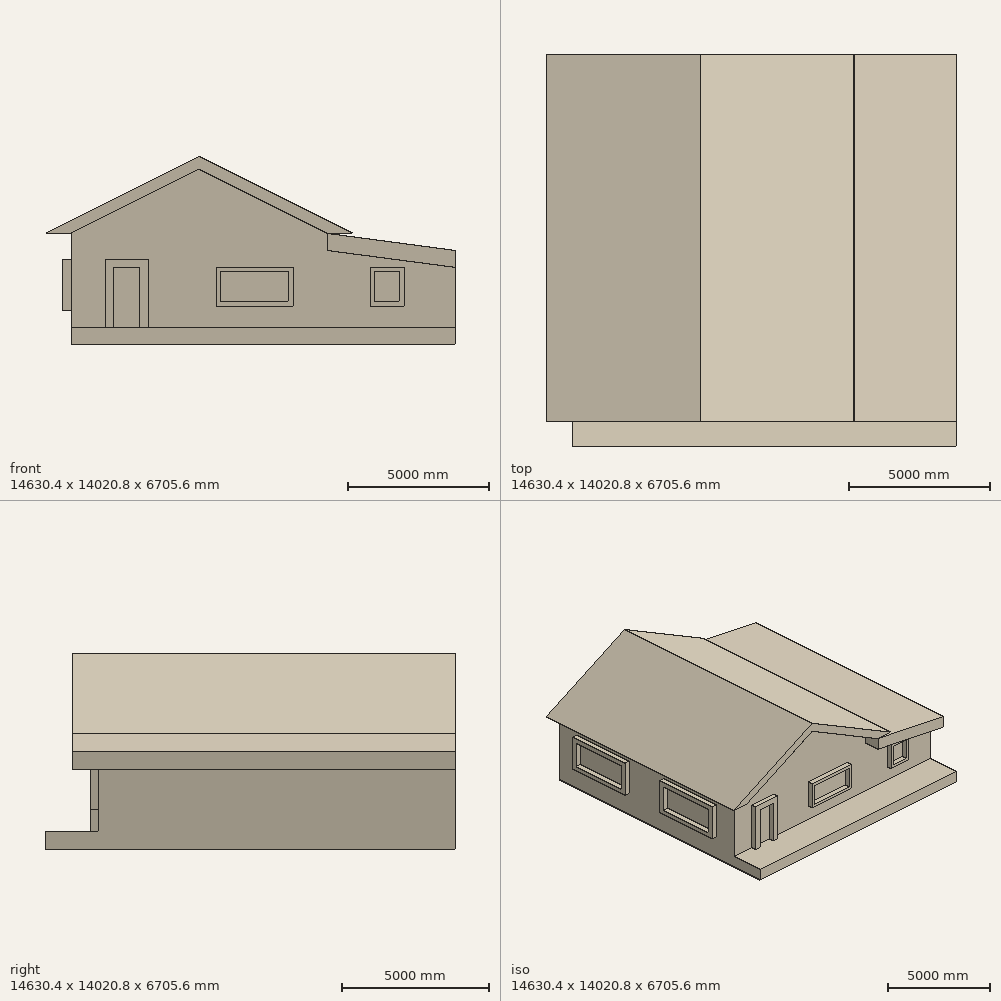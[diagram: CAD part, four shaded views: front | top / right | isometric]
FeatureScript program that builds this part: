
annotation { "Feature Type Name" : "Feature", "Feature Type Description" : "" }
export const myFeature = defineFeature(function(context is Context, id is Id, definition is map)
    precondition{}
    {
        {
            var Q0;
            Q0=qCreatedBy(makeId("Front.planeOp"),FACE);
            var sketch = newSketch(context, id + "F0", { "sketchPlane" : qUnion([Q0])});
            skLineSegment(sketch, "E0", {"start": v(0, 0) * mm, "end": v(-4572, 0) * mm});
            skLineSegment(sketch, "E1", {"start": v(0, 0) * mm, "end": v(4572, 0) * mm});
            skLineSegment(sketch, "E2", {"start": v(0, 0) * mm, "end": v(0, 2286) * mm});
            skLineSegment(sketch, "E3", {"start": v(0, 2286) * mm, "end": v(4572, 0) * mm});
            skLineSegment(sketch, "E4", {"start": v(0, 2286) * mm, "end": v(-4572, 0) * mm});
            skLineSegment(sketch, "E5", {"start": v(4572, 0) * mm, "end": v(5486.4, 0) * mm});
            skLineSegment(sketch, "E6", {"start": v(-4572, 0) * mm, "end": v(-5486.4, 0) * mm});
            skLineSegment(sketch, "E7", {"start": v(0, 2286) * mm, "end": v(0, 2743.2) * mm});
            skLineSegment(sketch, "E8", {"start": v(0, 2743.2) * mm, "end": v(5486.4, 0) * mm});
            skLineSegment(sketch, "E9", {"start": v(0, 2743.2) * mm, "end": v(-5486.4, 0) * mm});
            skLineSegment(sketch, "E10", {"start": v(4572, 0) * mm, "end": v(4572, -3352.8) * mm});
            skLineSegment(sketch, "E11", {"start": v(-4572, 0) * mm, "end": v(-4572, -3352.8) * mm});
            skLineSegment(sketch, "E12", {"start": v(-4572, -3352.8) * mm, "end": v(4572, -3352.8) * mm});
            skLineSegment(sketch, "E13", {"start": v(4572, -3352.8) * mm, "end": v(4572, -3962.4) * mm});
            skLineSegment(sketch, "E14", {"start": v(-4572, -3352.8) * mm, "end": v(-4572, -3962.4) * mm});
            skLineSegment(sketch, "E15", {"start": v(-4572, -3962.4) * mm, "end": v(4572, -3962.4) * mm});
            skLineSegment(sketch, "E16", {"start": v(4572, -3962.4) * mm, "end": v(9144, -3962.4) * mm});
            skLineSegment(sketch, "E17", {"start": v(4572, -3352.8) * mm, "end": v(9144, -3352.8) * mm});
            skLineSegment(sketch, "E18", {"start": v(9144, -3352.8) * mm, "end": v(9144, -3962.4) * mm});
            skLineSegment(sketch, "E19", {"start": v(9144, -3352.8) * mm, "end": v(9144, -609.6) * mm});
            skLineSegment(sketch, "E20", {"start": v(9144, -609.6) * mm, "end": v(4572, 0) * mm});
            skLineSegment(sketch, "E21", {"start": v(4572, -609.6) * mm, "end": v(9144, -1212.83) * mm});
            skLineSegment(sketch, "E22", {"start": v(-3048, -3352.8) * mm, "end": v(-3048, -1219.2) * mm});
            skLineSegment(sketch, "E23", {"start": v(-3048, -1219.2) * mm, "end": v(-2133.6, -1219.2) * mm});
            skLineSegment(sketch, "E24", {"start": v(-2133.6, -1219.2) * mm, "end": v(-2133.6, -3352.8) * mm});
            skLineSegment(sketch, "E25.0", {"start": v(-1828.8, -914.4) * mm, "end": v(-1828.8, -3352.8) * mm});
            skLineSegment(sketch, "E25.1", {"start": v(-3352.8, -914.4) * mm, "end": v(-1828.8, -914.4) * mm});
            skLineSegment(sketch, "E25.2", {"start": v(-3352.8, -3352.8) * mm, "end": v(-3352.8, -914.4) * mm});
            skLineSegment(sketch, "E26", {"start": v(609.6, -1219.2) * mm, "end": v(609.6, -2590.8) * mm});
            skLineSegment(sketch, "E27", {"start": v(609.6, -2590.8) * mm, "end": v(3352.8, -2590.8) * mm});
            skLineSegment(sketch, "E28", {"start": v(3352.8, -2590.8) * mm, "end": v(3352.8, -1219.2) * mm});
            skLineSegment(sketch, "E29", {"start": v(609.6, -1219.2) * mm, "end": v(3352.8, -1219.2) * mm});
            skLineSegment(sketch, "E30.0", {"start": v(3200.4, -2438.4) * mm, "end": v(3200.4, -1371.6) * mm});
            skLineSegment(sketch, "E30.1", {"start": v(762, -2438.4) * mm, "end": v(3200.4, -2438.4) * mm});
            skLineSegment(sketch, "E30.2", {"start": v(762, -1371.6) * mm, "end": v(762, -2438.4) * mm});
            skLineSegment(sketch, "E30.3", {"start": v(762, -1371.6) * mm, "end": v(3200.4, -1371.6) * mm});
            skLineSegment(sketch, "E31.bottom", {"start": v(6096, -1219.2) * mm, "end": v(7315.2, -1219.2) * mm});
            skLineSegment(sketch, "E31.top", {"start": v(6096, -2590.8) * mm, "end": v(7315.2, -2590.8) * mm});
            skLineSegment(sketch, "E31.left", {"start": v(6096, -1219.2) * mm, "end": v(6096, -2590.8) * mm});
            skLineSegment(sketch, "E31.right", {"start": v(7315.2, -1219.2) * mm, "end": v(7315.2, -2590.8) * mm});
            skLineSegment(sketch, "E32.0", {"start": v(6248.4, -1371.6) * mm, "end": v(7162.8, -1371.6) * mm});
            skLineSegment(sketch, "E32.1", {"start": v(6248.4, -1371.6) * mm, "end": v(6248.4, -2438.4) * mm});
            skLineSegment(sketch, "E32.2", {"start": v(6248.4, -2438.4) * mm, "end": v(7162.8, -2438.4) * mm});
            skLineSegment(sketch, "E32.3", {"start": v(7162.8, -1371.6) * mm, "end": v(7162.8, -2438.4) * mm});
            skSolve(sketch);
        }
        {
            var Q0;
            Q0=makeQuery(id+"F0.imprint","IMPRINT",FACE,{"disambiguationData":[TD([[makeQuery(id+"F0.imprint","IMPRINT",EDGE,{"derivedFrom":sQuery(id+"F0.wireOp",EDGE,"E4")}),-1.0]])]});
            var Q1;
            Q1=makeQuery(id+"F0.imprint","IMPRINT",FACE,{"disambiguationData":[TD([[makeQuery(id+"F0.imprint","IMPRINT",EDGE,{"derivedFrom":sQuery(id+"F0.wireOp",EDGE,"E3")}),1.0]])]});
            var Q2;
            {var subQ0=sQuery(id+"F0.wireOp",EDGE,"E20");Q2=makeQuery(id+"F0.imprint","IMPRINT",FACE,{"disambiguationData":[TD([[makeQuery(id+"F0.imprint","IMPRINT",EDGE,{"derivedFrom":subQ0}),1.0]])]});}
            extrude(context, id + "F1", {"entities" : qUnion([Q0, Q1, Q2]), "depth" : 914.4 * mm, "offsetDistance" : 30.48 * mm, "hasSecondDirection" : true, "secondDirectionOppositeDirection" : true, "secondDirectionDepth" : 12192 * mm});
        }
        {
            var Q0;
            Q0=makeQuery(id+"F0.imprint","IMPRINT",FACE,{"disambiguationData":[TD([[makeQuery(id+"F0.imprint","IMPRINT",EDGE,{"derivedFrom":sQuery(id+"F0.wireOp",EDGE,"E0")}),1.0]])]});
            var Q1;
            Q1=makeQuery(id+"F0.imprint","IMPRINT",FACE,{"disambiguationData":[TD([[makeQuery(id+"F0.imprint","IMPRINT",EDGE,{"derivedFrom":sQuery(id+"F0.wireOp",EDGE,"E0")}),-1.0]])]});
            var Q2;
            Q2=makeQuery(id+"F0.imprint","IMPRINT",FACE,{"disambiguationData":[TD([[makeQuery(id+"F0.imprint","IMPRINT",EDGE,{"derivedFrom":sQuery(id+"F0.wireOp",EDGE,"E1")}),1.0]])]});
            var Q3;
            {var subQ1=sQuery(id+"F0.wireOp",EDGE,"E17");Q3=makeQuery(id+"F0.imprint","IMPRINT",FACE,{"disambiguationData":[TD([[makeQuery(id+"F0.imprint","IMPRINT",EDGE,{"derivedFrom":subQ1}),1.0]])]});}
            extrude(context, id + "F2", {"entities" : qUnion([Q0, Q1, Q2, Q3]), "depth" : 30.48 * mm, "offsetDistance" : 30.48 * mm, "hasSecondDirection" : true, "secondDirectionOppositeDirection" : true, "secondDirectionDepth" : 12192 * mm});
        }
        {
            var Q0;
            {var subQ0=sQuery(id+"F0.wireOp",EDGE,"E22");Q0=makeQuery(id+"F0.imprint","IMPRINT",FACE,{"disambiguationData":[TD([[makeQuery(id+"F0.imprint","IMPRINT",EDGE,{"derivedFrom":subQ0}),1.0]])]});}
            extrude(context, id + "F3", {"entities" : qUnion([Q0]), "operationType" : NewBodyOperationType.ADD, "depth" : 304.8 * mm, "offsetDistance" : 30.48 * mm, "hasSecondDirection" : true, "secondDirectionOppositeDirection" : true, "secondDirectionDepth" : 12192 * mm});
        }
        {
            var Q0;
            Q0=makeQuery(id+"F0.imprint","IMPRINT",FACE,{"disambiguationData":[TD([[makeQuery(id+"F0.imprint","IMPRINT",EDGE,{"derivedFrom":sQuery(id+"F0.wireOp",EDGE,"E26")}),1.0]])]});
            var Q1;
            Q1=makeQuery(id+"F0.imprint","IMPRINT",FACE,{"disambiguationData":[TD([[makeQuery(id+"F0.imprint","IMPRINT",EDGE,{"derivedFrom":sQuery(id+"F0.wireOp",EDGE,"E31.bottom")}),-1.0]])]});
            extrude(context, id + "F4", {"entities" : qUnion([Q0, Q1]), "operationType" : NewBodyOperationType.ADD, "depth" : 304.8 * mm, "offsetDistance" : 30.48 * mm, "hasSecondDirection" : true, "secondDirectionOppositeDirection" : true, "secondDirectionDepth" : 12192 * mm});
        }
        {
            var Q0;
            {var subQ6=sQuery(id+"F0.wireOp",EDGE,"E13");Q0=makeQuery(id+"F0.imprint","IMPRINT",FACE,{"disambiguationData":[TD([[makeQuery(id+"F0.imprint","IMPRINT",EDGE,{"derivedFrom":subQ6}),-1.0]])]});}
            var Q1;
            Q1=makeQuery(id+"F0.imprint","IMPRINT",FACE,{"disambiguationData":[TD([[makeQuery(id+"F0.imprint","IMPRINT",EDGE,{"derivedFrom":sQuery(id+"F0.wireOp",EDGE,"E13")}),1.0]])]});
            extrude(context, id + "F5", {"entities" : qUnion([Q0, Q1]), "operationType" : NewBodyOperationType.ADD, "depth" : 1828.8 * mm, "offsetDistance" : 30.48 * mm, "hasSecondDirection" : true, "secondDirectionOppositeDirection" : true, "secondDirectionDepth" : 12192 * mm});
        }
        {
            var Q0;
            Q0=makeQuery(id+"F0.imprint","IMPRINT",FACE,{"disambiguationData":[TD([[makeQuery(id+"F0.imprint","IMPRINT",EDGE,{"derivedFrom":sQuery(id+"F0.wireOp",EDGE,"E32.0")}),-1.0]])]});
            var Q1;
            Q1=makeQuery(id+"F0.imprint","IMPRINT",FACE,{"disambiguationData":[TD([[makeQuery(id+"F0.imprint","IMPRINT",EDGE,{"derivedFrom":sQuery(id+"F0.wireOp",EDGE,"E30.0")}),1.0]])]});
            var Q2;
            {var subQ0=sQuery(id+"F0.wireOp",EDGE,"E22");Q2=makeQuery(id+"F0.imprint","IMPRINT",FACE,{"disambiguationData":[TD([[makeQuery(id+"F0.imprint","IMPRINT",EDGE,{"derivedFrom":subQ0}),-1.0]])]});}
            extrude(context, id + "F6", {"entities" : qUnion([Q0, Q1, Q2]), "operationType" : NewBodyOperationType.ADD, "depth" : 30.48 * mm, "offsetDistance" : 30.48 * mm, "hasSecondDirection" : true, "secondDirectionOppositeDirection" : true, "secondDirectionDepth" : 12192 * mm});
        }
        {
            var Q0;
            Q0=makeQuery(id+"F5.boolean.opBoolean","MERGE",FACE,{"derivedFrom":[makeQuery(id+"F2.opExtrude","SWEPT_FACE",FACE,{"disambiguationData":[OSD([sQuery(id+"F0.wireOp",EDGE,"E11")])]}),makeQuery(id+"F5.opExtrude","SWEPT_FACE",FACE,{"disambiguationData":[OSD([sQuery(id+"F0.wireOp",EDGE,"E14")])]})]});
            var sketch = newSketch(context, id + "F7", { "sketchPlane" : qUnion([Q0])});
            skLineSegment(sketch, "E33.bottom", {"start": v(-10972.8, -914.4) * mm, "end": v(-7315.2, -914.4) * mm});
            skLineSegment(sketch, "E33.top", {"start": v(-10972.8, -2743.2) * mm, "end": v(-7315.2, -2743.2) * mm});
            skLineSegment(sketch, "E33.left", {"start": v(-10972.8, -914.4) * mm, "end": v(-10972.8, -2743.2) * mm});
            skLineSegment(sketch, "E33.right", {"start": v(-7315.2, -914.4) * mm, "end": v(-7315.2, -2743.2) * mm});
            skLineSegment(sketch, "E34.left", {"start": v(-7315.2, -914.4) * mm, "end": v(-7315.2, -914.4) * mm});
            skLineSegment(sketch, "E34.right", {"start": v(-1219.2, -914.4) * mm, "end": v(-1219.2, -914.4) * mm});
            skLineSegment(sketch, "E35.bottom", {"start": v(-1219.2, -914.4) * mm, "end": v(-4876.8, -914.4) * mm});
            skLineSegment(sketch, "E35.top", {"start": v(-1219.2, -2743.2) * mm, "end": v(-4876.8, -2743.2) * mm});
            skLineSegment(sketch, "E35.left", {"start": v(-1219.2, -914.4) * mm, "end": v(-1219.2, -2743.2) * mm});
            skLineSegment(sketch, "E35.right", {"start": v(-4876.8, -914.4) * mm, "end": v(-4876.8, -2743.2) * mm});
            skLineSegment(sketch, "E36.0", {"start": v(-10728.96, -1158.24) * mm, "end": v(-7559.04, -1158.24) * mm});
            skLineSegment(sketch, "E36.1", {"start": v(-10728.96, -1158.24) * mm, "end": v(-10728.96, -2499.36) * mm});
            skLineSegment(sketch, "E36.2", {"start": v(-10728.96, -2499.36) * mm, "end": v(-7559.04, -2499.36) * mm});
            skLineSegment(sketch, "E36.3", {"start": v(-7559.04, -1158.24) * mm, "end": v(-7559.04, -2499.36) * mm});
            skLineSegment(sketch, "E37.0", {"start": v(-1463.04, -1158.24) * mm, "end": v(-4632.96, -1158.24) * mm});
            skLineSegment(sketch, "E37.1", {"start": v(-1463.04, -1158.24) * mm, "end": v(-1463.04, -2499.36) * mm});
            skLineSegment(sketch, "E37.2", {"start": v(-1463.04, -2499.36) * mm, "end": v(-4632.96, -2499.36) * mm});
            skLineSegment(sketch, "E37.3", {"start": v(-4632.96, -1158.24) * mm, "end": v(-4632.96, -2499.36) * mm});
            skSolve(sketch);
        }
        {
            var Q0;
            Q0=makeQuery(id+"F7.imprint","IMPRINT",FACE,{"disambiguationData":[TD([[makeQuery(id+"F7.imprint","IMPRINT",EDGE,{"derivedFrom":sQuery(id+"F7.wireOp",EDGE,"E35.bottom")}),1.0]])]});
            var Q1;
            Q1=makeQuery(id+"F7.imprint","IMPRINT",FACE,{"disambiguationData":[TD([[makeQuery(id+"F7.imprint","IMPRINT",EDGE,{"derivedFrom":sQuery(id+"F7.wireOp",EDGE,"E33.bottom")}),-1.0]])]});
            extrude(context, id + "F8", {"entities" : qUnion([Q0, Q1]), "operationType" : NewBodyOperationType.ADD, "depth" : 304.8 * mm, "offsetDistance" : 30.48 * mm});
        }
    });
